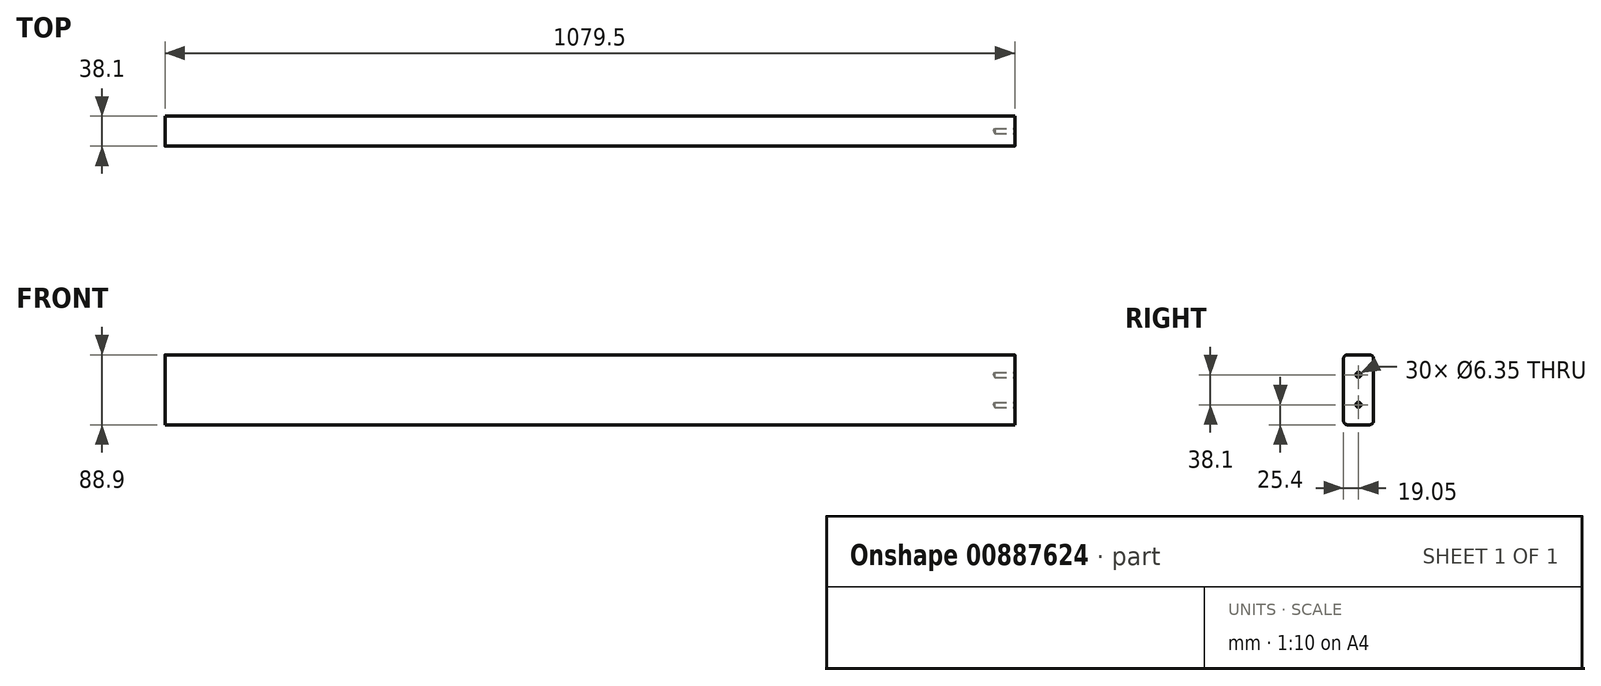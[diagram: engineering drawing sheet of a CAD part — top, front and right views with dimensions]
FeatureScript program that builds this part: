
annotation { "Feature Type Name" : "Feature", "Feature Type Description" : "" }
export const myFeature = defineFeature(function(context is Context, id is Id, definition is map)
    precondition{}
    {
        {
            var Q0;
            Q0=qCreatedBy(makeId("Right.planeOp"),FACE);
            var sketch = newSketch(context, id + "F0", { "sketchPlane" : qUnion([Q0])});
            skLineSegment(sketch, "E0.bottom", {"start": v(19.05, 44.45) * mm, "end": v(-19.05, 44.45) * mm});
            skLineSegment(sketch, "E0.top", {"start": v(19.05, -44.45) * mm, "end": v(-19.05, -44.45) * mm});
            skLineSegment(sketch, "E0.left", {"start": v(19.05, 44.45) * mm, "end": v(19.05, -44.45) * mm});
            skLineSegment(sketch, "E0.right", {"start": v(-19.05, 44.45) * mm, "end": v(-19.05, -44.45) * mm});
            skPoint(sketch, "E0.middle", {"position": v(0, 0) * mm});
            skSolve(sketch);
        }
        {
            var Q0;
            Q0=makeQuery(id+"F0.imprint","IMPRINT",FACE,{"disambiguationData":[TD([[makeQuery(id+"F0.imprint","IMPRINT",EDGE,{"derivedFrom":sQuery(id+"F0.wireOp",EDGE,"E0.bottom")}),1.0]])]});
            extrude(context, id + "F1", {"entities" : qUnion([Q0]), "endBound" : BoundingType.SYMMETRIC, "depth" : 1079.5 * mm, "offsetDistance" : 25.4 * mm});
        }
        {
            var Q0;
            Q0=makeQuery(id+"F1.opExtrude","SWEPT_EDGE",EDGE,{"disambiguationData":[OSD([sQuery(id+"F0.wireOp",EDGE,"E0.bottom"),sQuery(id+"F0.wireOp",EDGE,"E0.right")])]});
            var Q1;
            Q1=makeQuery(id+"F1.opExtrude","SWEPT_EDGE",EDGE,{"disambiguationData":[OSD([sQuery(id+"F0.wireOp",EDGE,"E0.bottom"),sQuery(id+"F0.wireOp",EDGE,"E0.left")])]});
            var Q2;
            Q2=makeQuery(id+"F1.opExtrude","SWEPT_EDGE",EDGE,{"disambiguationData":[OSD([sQuery(id+"F0.wireOp",EDGE,"E0.top"),sQuery(id+"F0.wireOp",EDGE,"E0.right")])]});
            var Q3;
            Q3=makeQuery(id+"F1.opExtrude","SWEPT_EDGE",EDGE,{"disambiguationData":[OSD([sQuery(id+"F0.wireOp",EDGE,"E0.top"),sQuery(id+"F0.wireOp",EDGE,"E0.left")])]});
            fillet(context, id + "F2", {"entities" : qUnion([Q0, Q1, Q2, Q3]), "radius" : 5.08 * mm, "tangentPropagation" : true, "allowEdgeOverflow" : false});
        }
        {
            var Q0;
            Q0=makeQuery(id+"F1.opExtrude","CAP_FACE",FACE,{"disambiguationData":[OSD([sQuery(id+"F0.wireOp",EDGE,"E0.bottom"),sQuery(id+"F0.wireOp",EDGE,"E0.top"),sQuery(id+"F0.wireOp",EDGE,"E0.left"),sQuery(id+"F0.wireOp",EDGE,"E0.right")])],"isStart":false});
            var sketch = newSketch(context, id + "F3", { "sketchPlane" : qUnion([Q0])});
            skPoint(sketch, "E1", {"position": v(0, 19.05) * mm});
            skPoint(sketch, "E2", {"position": v(0, -19.05) * mm});
            skSolve(sketch);
        }
        {
            var Q0;
            Q0=sQuery(id+"F3.wireOp",VERTEX,"E1");
            var Q1;
            Q1=sQuery(id+"F3.wireOp",VERTEX,"E2");
            var Q2;
            Q2=makeQuery(id+"F1.opExtrude","SWEPT_BODY",BODY,{"disambiguationData":[OSD([sQuery(id+"F0.wireOp",EDGE,"E0.bottom"),sQuery(id+"F0.wireOp",EDGE,"E0.top"),sQuery(id+"F0.wireOp",EDGE,"E0.left"),sQuery(id+"F0.wireOp",EDGE,"E0.right")])]});
            hole(context, id + "F4", {"style" : HoleStyle.SIMPLE, "endStyle" : HoleEndStyle.BLIND, "holeDiameter" : 6.35 * mm, "majorDiameter" : 6.35 * mm, "holeDepth" : 25.4 * mm, "isTappedThrough" : true, "tappedDepth" : 12.7 * mm, "tapClearance" : 3, "locations" : qUnion([Q0, Q1]), "scope" : qUnion([Q2])});
        }
    });
